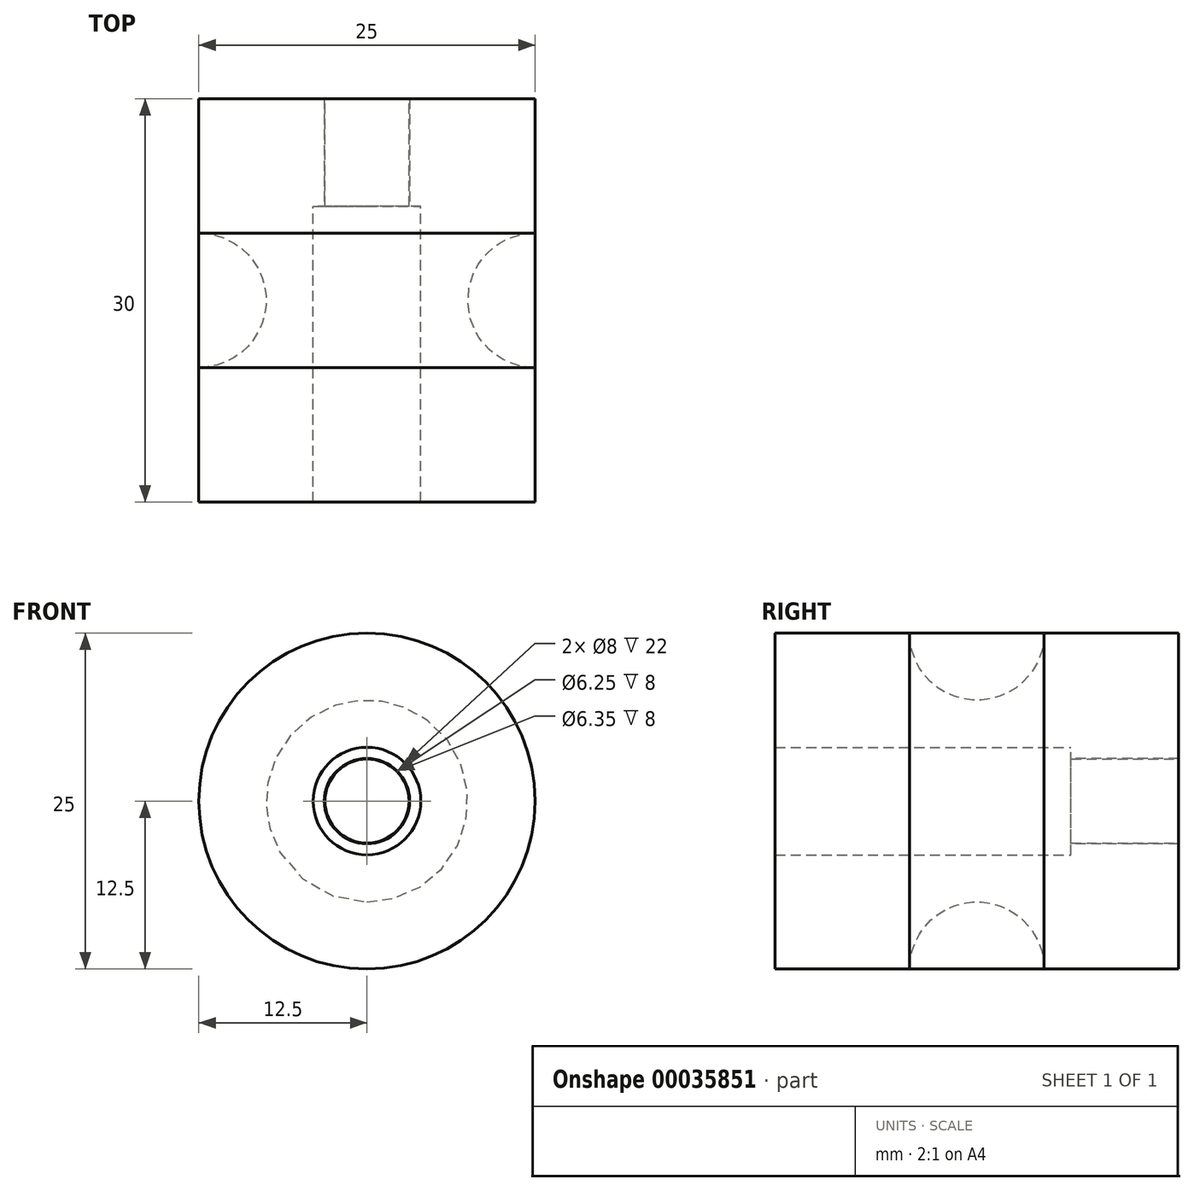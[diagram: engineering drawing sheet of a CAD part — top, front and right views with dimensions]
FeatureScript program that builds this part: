
annotation { "Feature Type Name" : "Feature", "Feature Type Description" : "" }
export const myFeature = defineFeature(function(context is Context, id is Id, definition is map)
    precondition{}
    {
        {
            var Q0;
            Q0=qCreatedBy(makeId("Front.planeOp"),FACE);
            var sketch = newSketch(context, id + "F0", { "sketchPlane" : qUnion([Q0])});
            skCircle(sketch, "E0", {"center": v(0, 0) * mm, "radius": 12.5 * mm});
            skCircle(sketch, "E1", {"center": v(0, 0) * mm, "radius": 3.12 * mm});
            skSolve(sketch);
        }
        {
            var Q0;
            Q0=makeQuery(id+"F0.imprint","IMPRINT",FACE,{"disambiguationData":[TD([[makeQuery(id+"F0.imprint","IMPRINT",EDGE,{"derivedFrom":sQuery(id+"F0.wireOp",EDGE,"E0")}),1.0]])]});
            extrude(context, id + "F1", {"entities" : qUnion([Q0]), "depth" : 30 * mm});
        }
        {
            var Q0;
            Q0=qCreatedBy(makeId("Front.planeOp"),FACE);
            cPlane(context, id + "F2", {"entities" : qUnion([Q0]), "cplaneType" : CPlaneType.OFFSET, "offset" : 8 * mm, "width" : 150 * mm, "height" : 150 * mm});
        }
        {
            var Q0;
            Q0=qCreatedBy(id+"F2.planeOp",FACE);
            var sketch = newSketch(context, id + "F3", { "sketchPlane" : qUnion([Q0])});
            skCircle(sketch, "E2", {"center": v(0, 0) * mm, "radius": 4 * mm});
            skCircle(sketch, "E3", {"center": v(0, 0) * mm, "radius": 12.5 * mm, "construction": true});
            skSolve(sketch);
        }
        {
            var Q0;
            Q0=makeQuery(id+"F3.imprint","IMPRINT",FACE,{"disambiguationData":[TD([[makeQuery(id+"F3.imprint","IMPRINT",EDGE,{"derivedFrom":sQuery(id+"F3.wireOp",EDGE,"E2")}),1.0]])]});
            var Q1;
            Q1=makeQuery(id+"F1.opExtrude","CAP_FACE",FACE,{"disambiguationData":[OSD([sQuery(id+"F0.wireOp",EDGE,"E0"),sQuery(id+"F0.wireOp",EDGE,"E1")])],"isStart":false});
            extrude(context, id + "F4", {"entities" : qUnion([Q0]), "operationType" : NewBodyOperationType.REMOVE, "endBound" : BoundingType.UP_TO_SURFACE, "endBoundEntityFace" : qUnion([Q1]), "depth" : 25 * mm});
        }
        {
            var Q0;
            Q0=qCreatedBy(makeId("Right.planeOp"),FACE);
            var sketch = newSketch(context, id + "F5", { "sketchPlane" : qUnion([Q0])});
            skLineSegment(sketch, "E4.0", {"start": v(-30, -12.5) * mm, "end": v(-30, 12.5) * mm, "construction": true});
            skLineSegment(sketch, "E5", {"start": v(-30, 12.5) * mm, "end": v(-30, 4) * mm});
            skLineSegment(sketch, "E6", {"start": v(0, -12.5) * mm, "end": v(-30, -12.5) * mm, "construction": true});
            skLineSegment(sketch, "E7", {"start": v(-30, 12.5) * mm, "end": v(-20, 12.5) * mm});
            skLineSegment(sketch, "E8", {"start": v(0, 12.5) * mm, "end": v(-10, 12.5) * mm});
            skLineSegment(sketch, "E9", {"start": v(0, 12.5) * mm, "end": v(0, 3.17) * mm});
            skLineSegment(sketch, "E10", {"start": v(0, 3.17) * mm, "end": v(-8, 3.17) * mm});
            skLineSegment(sketch, "E11", {"start": v(-8, 3.17) * mm, "end": v(-8, 4) * mm});
            skLineSegment(sketch, "E12", {"start": v(-8, 4) * mm, "end": v(-30, 4) * mm});
            skArc(sketch, "E13", {"start": v(-20, 12.5) * mm, "mid": v(-15, 7.5) * mm, "end": v(-10, 12.5) * mm});
            skLineSegment(sketch, "E14.trimOffspring", {"start": v(-20, 12.5) * mm, "end": v(-30, 12.5) * mm});
            skLineSegment(sketch, "E15.trimOffspring", {"start": v(-10, 12.5) * mm, "end": v(0, 12.5) * mm});
            skLineSegment(sketch, "E16", {"start": v(-30, 0) * mm, "end": v(-0.06, 0) * mm, "construction": true});
            skPoint(sketch, "E16.endSnap0", {"position": v(-30, 0) * mm});
            skSolve(sketch);
        }
        {
            var Q0;
            Q0=makeQuery(id+"F5.imprint","IMPRINT",FACE,{"disambiguationData":[TD([[makeQuery(id+"F5.imprint","IMPRINT",EDGE,{"derivedFrom":sQuery(id+"F5.wireOp",EDGE,"E5")}),1.0]])]});
            var Q1;
            Q1=sQuery(id+"F5.wireOp",EDGE,"E16");
            revolve(context, id + "F6", {"entities" : qUnion([Q0]), "axis" : qUnion([Q1]), "revolveType" : RevolveType.FULL});
        }
    });
